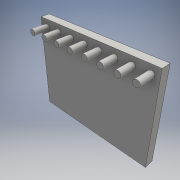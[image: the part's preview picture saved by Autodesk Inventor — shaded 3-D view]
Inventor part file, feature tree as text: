
AUTODESK INVENTOR PART (.ipt)
format: ipt  version: 2016 (Build 200138000, 138)  size: 118,784 bytes
history: native  units: mm
features: extrude x2, sketch x2, projected_geometry x1
ambient origin geometry x8: Origin, YZ Plane, XZ Plane, XY Plane, X Axis, Y Axis, Z Axis, Center Point
bodies: Body1 (feature_tree)
feature tree (5):
  extrude  "Extrusion2"  Depth=15.25mm
  extrude  "Extrusion3"  Depth=4.0mm
  sketch  "Sketch4"  dims[d9=20.25mm d10=15.25mm]
  sketch  "Sketch5"  dims[d11=1.5mm d12=0.0mm d13=1.0mm d20=0.5mm d21=4.0mm d22=0.0mm d23=0.0mm]
  projected_geometry  "Projected Loop2"
